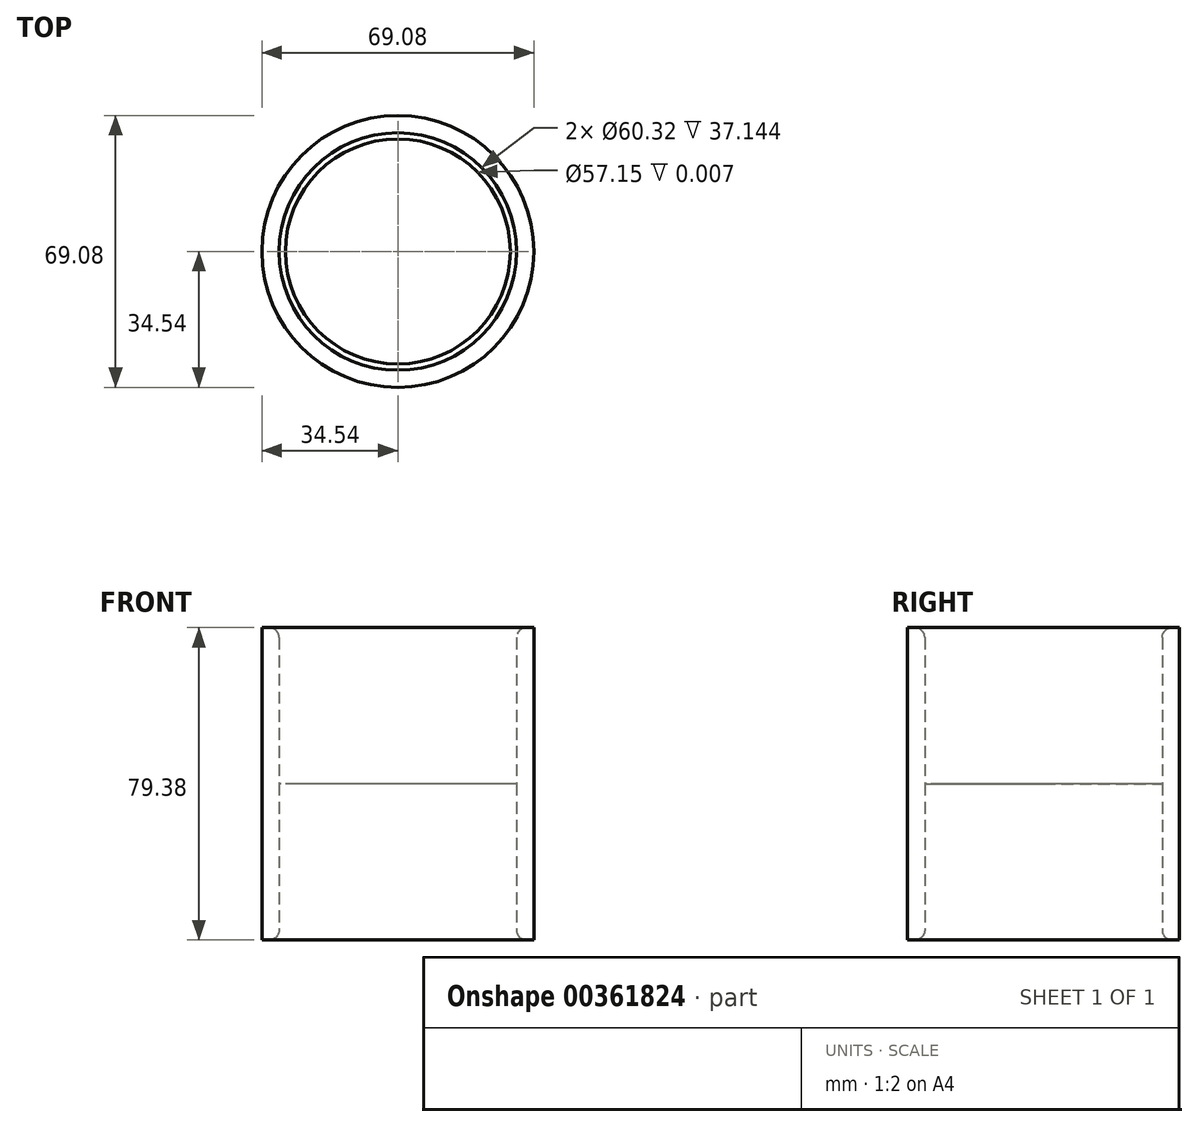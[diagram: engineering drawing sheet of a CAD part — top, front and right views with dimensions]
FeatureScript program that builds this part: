
annotation { "Feature Type Name" : "Feature", "Feature Type Description" : "" }
export const myFeature = defineFeature(function(context is Context, id is Id, definition is map)
    precondition{}
    {
        {
            var Q0;
            Q0=qCreatedBy(makeId("Top.planeOp"),FACE);
            var sketch = newSketch(context, id + "F0", { "sketchPlane" : qUnion([Q0])});
            skCircle(sketch, "E0", {"center": v(0, 0) * mm, "radius": 30.16 * mm});
            skCircle(sketch, "E1", {"center": v(0, 0) * mm, "radius": 34.54 * mm});
            skCircle(sketch, "E2", {"center": v(0, 0) * mm, "radius": 28.58 * mm});
            skSolve(sketch);
        }
        {
            var Q0;
            Q0=makeQuery(id+"F0.imprint","IMPRINT",FACE,{"disambiguationData":[TD([[makeQuery(id+"F0.imprint","IMPRINT",EDGE,{"derivedFrom":sQuery(id+"F0.wireOp",EDGE,"E0")}),-1.0]])]});
            extrude(context, id + "F1", {"entities" : qUnion([Q0]), "offsetDistance" : 25 * mm, "depth" : 79.38 * mm / 2, "hasSecondDirection" : true, "secondDirectionOppositeDirection" : true, "secondDirectionDepth" : 39.69 * mm});
        }
        {
            var Q0;
            Q0=makeQuery(id+"F0.imprint","IMPRINT",FACE,{"disambiguationData":[TD([[makeQuery(id+"F0.imprint","IMPRINT",EDGE,{"derivedFrom":sQuery(id+"F0.wireOp",EDGE,"E0")}),1.0]])]});
            extrude(context, id + "F2", {"entities" : qUnion([Q0]), "operationType" : NewBodyOperationType.ADD, "depth" : ((3.38 / 2) - 1.5) / 50.8 * mm, "hasSecondDirection" : true, "secondDirectionOppositeDirection" : true, "secondDirectionDepth" : ((3.38 / 2) - 1.5) / 50.8 * mm});
        }
        {
            var Q0;
            Q0=makeQuery(id+"F1.opExtrude","CAP_EDGE",EDGE,{"disambiguationData":[OSD([sQuery(id+"F0.wireOp",EDGE,"E0")])],"isStart":false});
            var Q1;
            Q1=makeQuery(id+"F1.opExtrude","CAP_EDGE",EDGE,{"disambiguationData":[OSD([sQuery(id+"F0.wireOp",EDGE,"E0")])],"isStart":true});
            fillet(context, id + "F3", {"entities" : qUnion([Q0, Q1]), "radius" : 2.54 * mm, "tangentPropagation" : true, "allowEdgeOverflow" : false});
        }
    });
